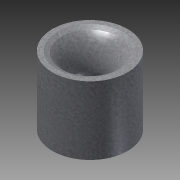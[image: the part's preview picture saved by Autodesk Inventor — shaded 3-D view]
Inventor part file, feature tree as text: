
AUTODESK INVENTOR PART (.ipt)
format: ipt  version: 2015 (Build 190159000, 159)  size: 177,664 bytes
history: native  units: in
note: dims shown in document units (in); Inventor stores cm internally (conversion verified against a paired STEP export)
features: revolve x1, sketch x1
ambient origin geometry x8: Origin, YZ Plane, XZ Plane, XY Plane, X Axis, Y Axis, Z Axis, Center Point
bodies: Solid1 (feature_tree)
feature tree (2):
  revolve  "Revolution1"  [1 undecoded]
  sketch  "Sketch1"  dims[d25=90.0deg d56=0.75in d57=1.0in d58=0.2185in d59=2.594in d60=0.5in d61=0.5in d62=1.75in d63=0.25in d64=105.0deg d65=0.5in d66=0.5in d67=0.25in d68=0.375in d69=2.0in d70=0.5in d71=0.25in d72=0.234in d73=0.25in d74=2.0in d75=0.25in d76=105.0deg d77=0.125in d78=0.25in d79=2.3995in d80=0.125in d81=0.25in d82=1.0in d83=0.1718in d84=1.6531in d85=1.2713in d86=90.0deg d87=3.1729in]
note: 1 required parameter value undecoded (feature->parameter linkage not recoverable at this tier; creation-order binding heuristic only, values carry confidence <= 0.55)
